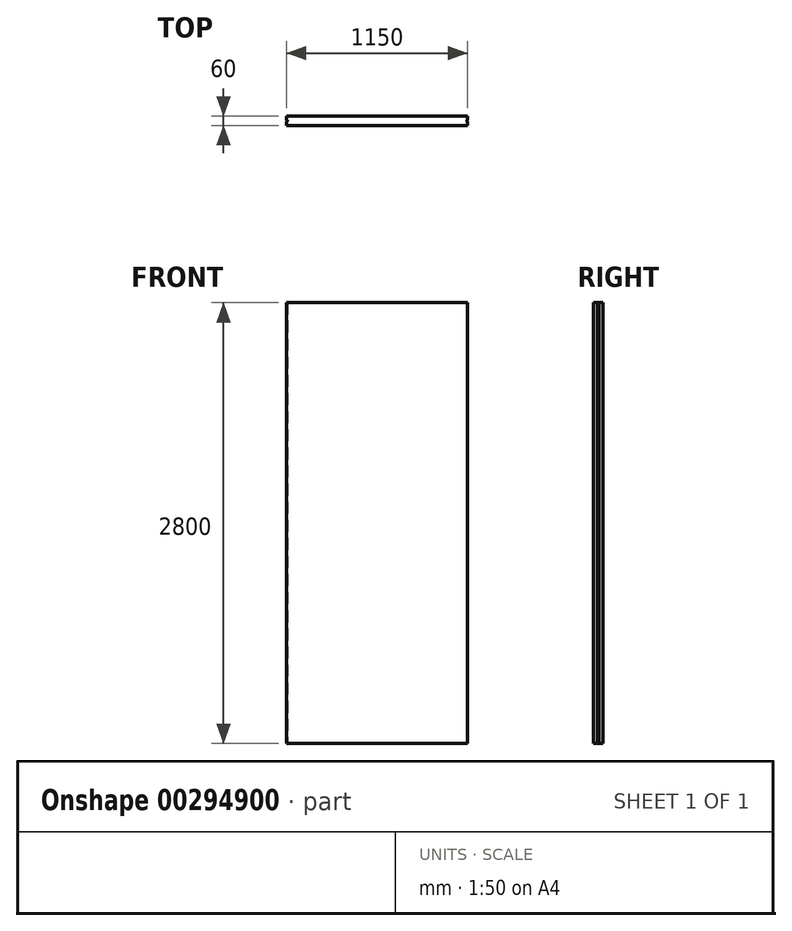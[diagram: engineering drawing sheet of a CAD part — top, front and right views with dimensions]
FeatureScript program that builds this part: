
annotation { "Feature Type Name" : "Feature", "Feature Type Description" : "" }
export const myFeature = defineFeature(function(context is Context, id is Id, definition is map)
    precondition{}
    {
        {
            var Q0;
            Q0=qCreatedBy(makeId("Top.planeOp"),FACE);
            var sketch = newSketch(context, id + "F0", { "sketchPlane" : qUnion([Q0])});
            skLineSegment(sketch, "E0.bottom", {"start": v(0, 0) * mm, "end": v(1150, 0) * mm});
            skLineSegment(sketch, "E0.top", {"start": v(0, 60) * mm, "end": v(1150, 60) * mm});
            skLineSegment(sketch, "E0.left", {"start": v(0, 0) * mm, "end": v(0, 60) * mm});
            skLineSegment(sketch, "E0.right", {"start": v(1150, 0) * mm, "end": v(1150, 60) * mm});
            skCircle(sketch, "E1", {"center": v(0, 30) * mm, "radius": 5 * mm});
            skCircle(sketch, "E2", {"center": v(1150, 30) * mm, "radius": 5 * mm});
            skSolve(sketch);
        }
        {
            var Q0;
            {var subQ1=sQuery(id+"F0.wireOp",EDGE,"E0.bottom");Q0=makeQuery(id+"F0.imprint","IMPRINT",FACE,{"disambiguationData":[TD([[makeQuery(id+"F0.imprint","IMPRINT",EDGE,{"derivedFrom":subQ1}),1.0]])]});}
            extrude(context, id + "F1", {"entities" : qUnion([Q0]), "depth" : 2800 * mm, "offsetDistance" : 25.4 * mm});
        }
    });
